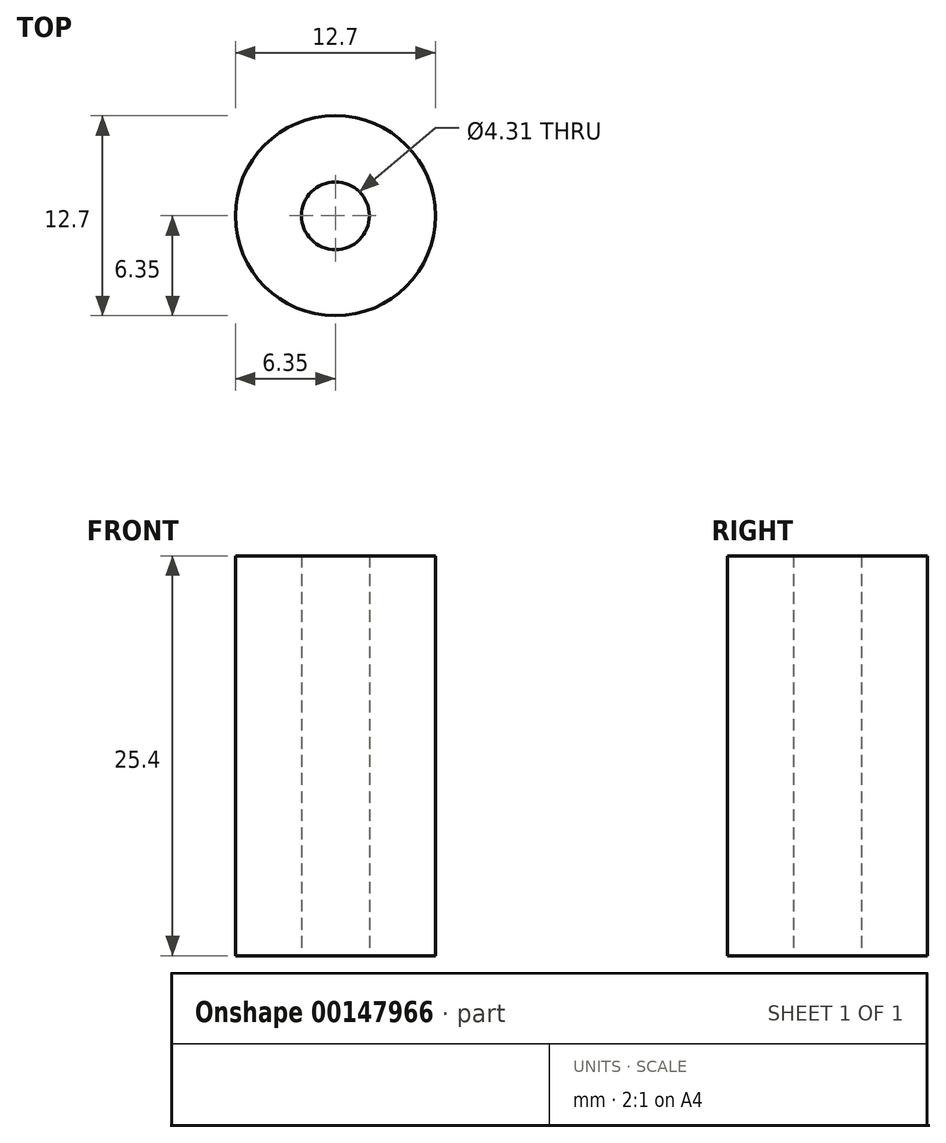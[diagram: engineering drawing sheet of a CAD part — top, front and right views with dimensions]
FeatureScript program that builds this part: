
annotation { "Feature Type Name" : "Feature", "Feature Type Description" : "" }
export const myFeature = defineFeature(function(context is Context, id is Id, definition is map)
    precondition{}
    {
        {
            var Q0;
            Q0=qCreatedBy(makeId("Top.planeOp"),FACE);
            var sketch = newSketch(context, id + "F0", { "sketchPlane" : qUnion([Q0])});
            skCircle(sketch, "E0", {"center": v(0, 0) * mm, "radius": 6.35 * mm});
            skCircle(sketch, "E1", {"center": v(0, 0) * mm, "radius": 2.15 * mm});
            skSolve(sketch);
        }
        {
            var Q0;
            Q0=qSketchRegion(id+"F0",true);
            extrude(context, id + "F1", {"entities" : qUnion([Q0]), "depth" : 25.4 * mm});
        }
    });
